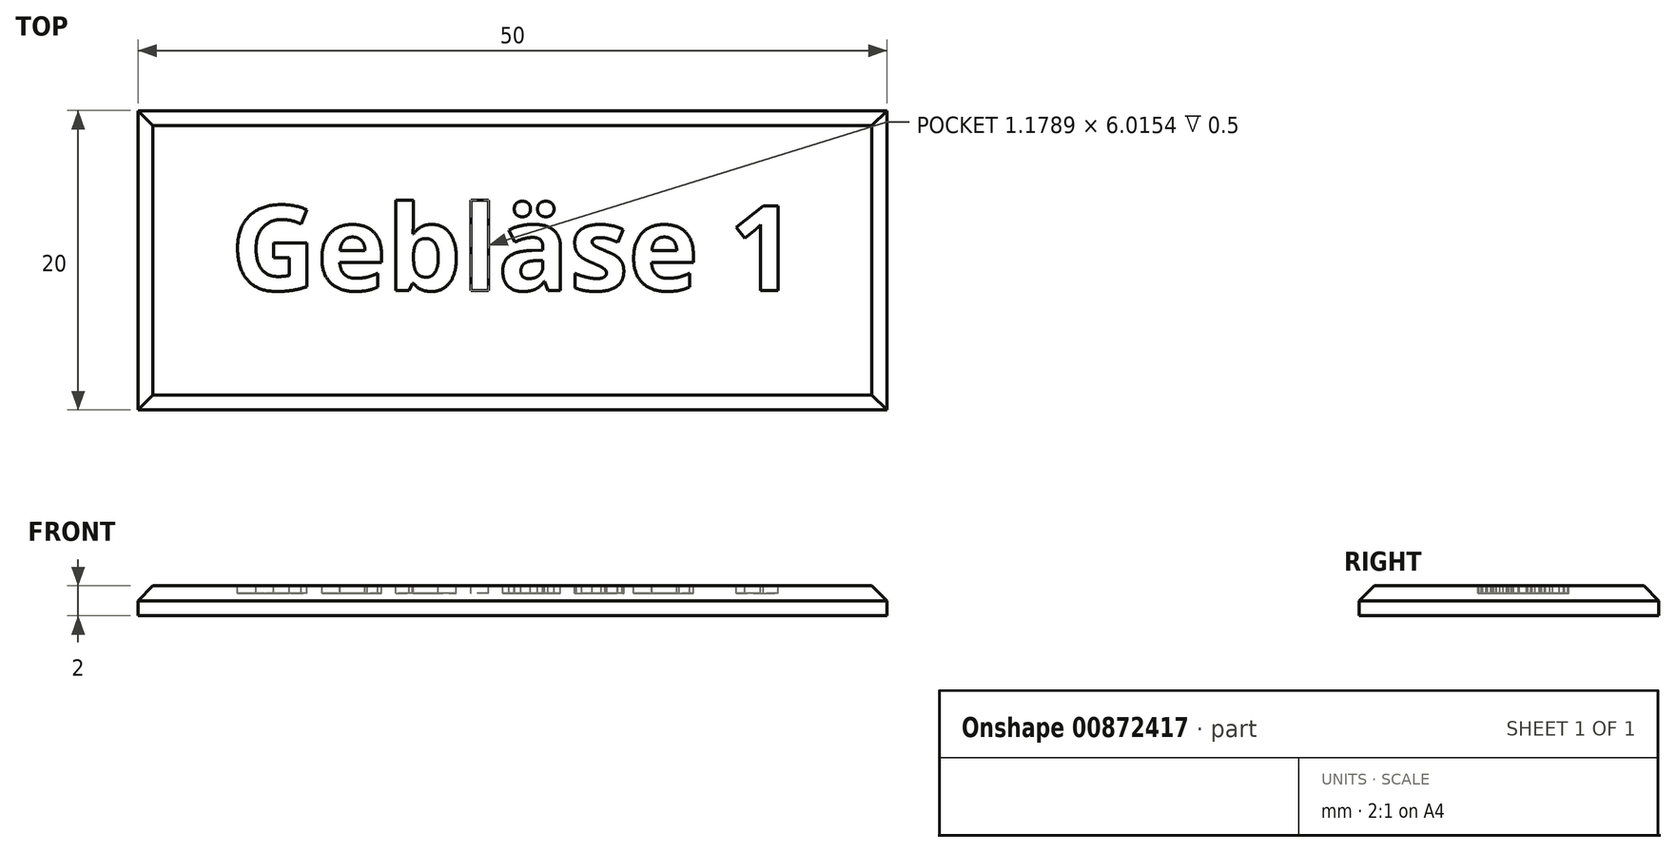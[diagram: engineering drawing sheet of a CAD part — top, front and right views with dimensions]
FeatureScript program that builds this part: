
annotation { "Feature Type Name" : "Feature", "Feature Type Description" : "" }
export const myFeature = defineFeature(function(context is Context, id is Id, definition is map)
    precondition{}
    {
        {
            var Q0;
            Q0=qCreatedBy(makeId("Top.planeOp"),FACE);
            var sketch = newSketch(context, id + "F0", { "sketchPlane" : qUnion([Q0])});
            skLineSegment(sketch, "E0.bottom", {"start": v(-55.8, 45.3) * mm, "end": v(-5.8, 45.3) * mm});
            skLineSegment(sketch, "E0.top", {"start": v(-55.8, 25.3) * mm, "end": v(-5.8, 25.3) * mm});
            skLineSegment(sketch, "E0.left", {"start": v(-55.8, 45.3) * mm, "end": v(-55.8, 25.3) * mm});
            skLineSegment(sketch, "E0.right", {"start": v(-5.8, 45.3) * mm, "end": v(-5.8, 25.3) * mm});
            skSolve(sketch);
        }
        {
            var Q0;
            Q0 = qSketchRegion(id + "F0", true);
            extrude(context, id + "F1", {"entities" : qUnion([Q0]), "depth" : 2 * mm, "offsetDistance" : 25 * mm});
        }
        {
            var Q0;
            Q0=makeQuery(id+"F1.opExtrude","CAP_FACE",FACE,{"disambiguationData":[OSD([sQuery(id+"F0.wireOp",EDGE,"E0.bottom"),sQuery(id+"F0.wireOp",EDGE,"E0.top"),sQuery(id+"F0.wireOp",EDGE,"E0.left"),sQuery(id+"F0.wireOp",EDGE,"E0.right")])],"isStart":false});
            var sketch = newSketch(context, id + "F2", { "sketchPlane" : qUnion([Q0])});
            skText(sketch, "E1", { "text": "Gebläse 1", "fontName": "OpenSans-Bold.ttf"});
            const initialGuessF2  = {"E1": [-0.04961, 0.03329, 1, 0, 0.0057]};
            skSetInitialGuess(sketch, initialGuessF2);
            skSolve(sketch);
        }
        {
            var Q0;
            Q0 = qSketchRegion(id + "F2", true);
            extrude(context, id + "F3", {"entities" : qUnion([Q0]), "operationType" : NewBodyOperationType.REMOVE, "oppositeDirection" : true, "depth" : 0.5 * mm, "offsetDistance" : 25 * mm});
        }
        {
            var Q0;
            Q0=makeQuery(id+"F1.opExtrude","CAP_EDGE",EDGE,{"disambiguationData":[OSD([sQuery(id+"F0.wireOp",EDGE,"E0.bottom")])],"isStart":false});
            var Q1;
            Q1=makeQuery(id+"F1.opExtrude","CAP_EDGE",EDGE,{"disambiguationData":[OSD([sQuery(id+"F0.wireOp",EDGE,"E0.left")])],"isStart":false});
            var Q2;
            Q2=makeQuery(id+"F1.opExtrude","CAP_EDGE",EDGE,{"disambiguationData":[OSD([sQuery(id+"F0.wireOp",EDGE,"E0.top")])],"isStart":false});
            var Q3;
            Q3=makeQuery(id+"F1.opExtrude","CAP_EDGE",EDGE,{"disambiguationData":[OSD([sQuery(id+"F0.wireOp",EDGE,"E0.right")])],"isStart":false});
            chamfer(context, id + "F4", {"entities" : qUnion([Q0, Q1, Q2, Q3]), "width" : 1 * mm, "tangentPropagation" : true});
        }
    });
